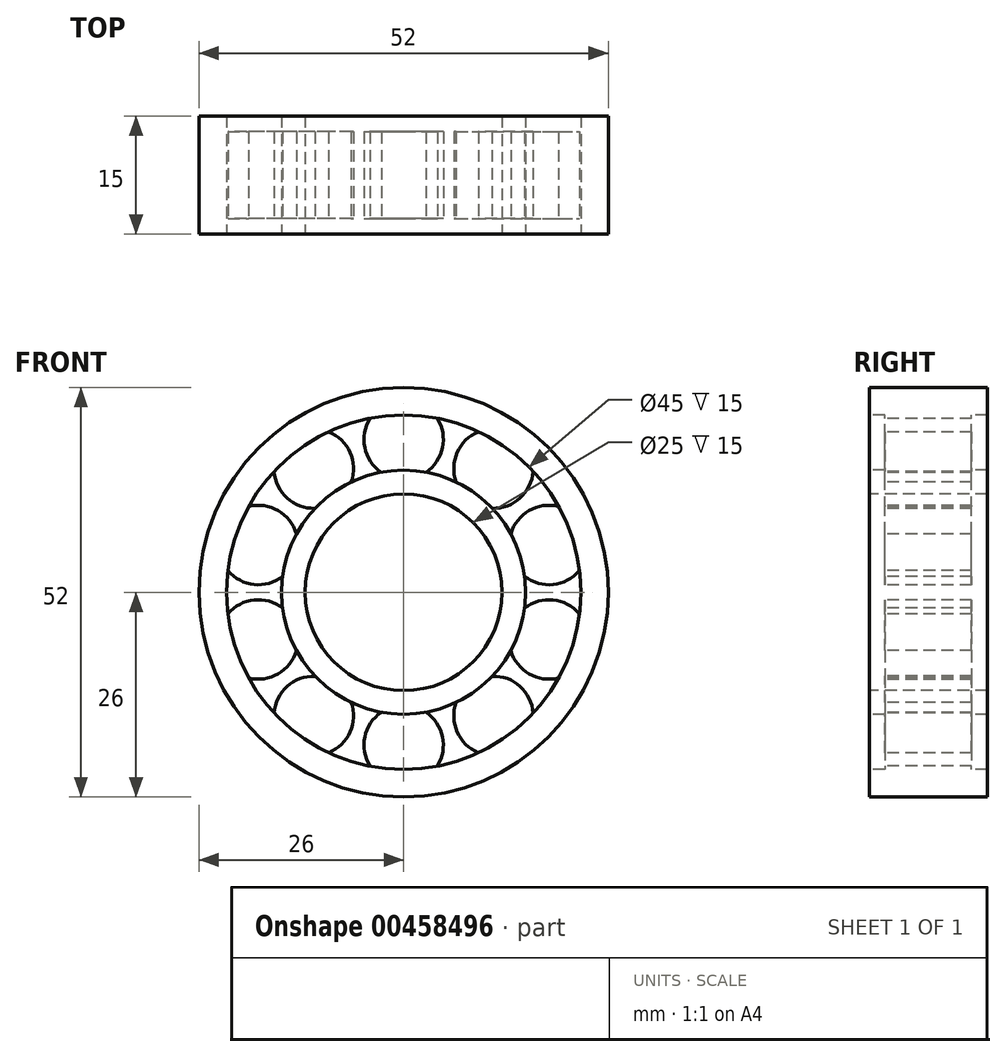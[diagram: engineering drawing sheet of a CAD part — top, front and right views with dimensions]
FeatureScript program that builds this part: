
annotation { "Feature Type Name" : "Feature", "Feature Type Description" : "" }
export const myFeature = defineFeature(function(context is Context, id is Id, definition is map)
    precondition{}
    {
        {
            var Q0;
            Q0=qCreatedBy(makeId("Front.planeOp"),FACE);
            var sketch = newSketch(context, id + "F0", { "sketchPlane" : qUnion([Q0])});
            skCircle(sketch, "E0", {"center": v(0, 0) * mm, "radius": 12.5 * mm});
            skCircle(sketch, "E1", {"center": v(0, 0) * mm, "radius": 26 * mm});
            skLineSegment(sketch, "E2.anchor2", {"start": v(0, -14.42) * mm, "end": v(0, -15.5) * mm, "construction": true});
            skPoint(sketch, "E3.orphan", {"position": v(9.11, 12.54) * mm});
            skPoint(sketch, "E4.orphan", {"position": v(14.74, 4.79) * mm});
            skPoint(sketch, "E5.orphan", {"position": v(14.74, -4.79) * mm});
            skPoint(sketch, "E6.orphan", {"position": v(9.11, -12.54) * mm});
            skPoint(sketch, "E7.orphan", {"position": v(0, -22.5) * mm});
            skPoint(sketch, "E8.orphan", {"position": v(0, 22.5) * mm});
            skPoint(sketch, "E2.anchor1.end.orphan", {"position": v(0, 15.5) * mm});
            skCircle(sketch, "E9", {"center": v(0, 0) * mm, "radius": 15.5 * mm});
            skCircle(sketch, "E10", {"center": v(0, 0) * mm, "radius": 22.5 * mm});
            skSolve(sketch);
        }
        {
            var Q0;
            Q0=makeQuery(id+"F0.imprint","IMPRINT",FACE,{"disambiguationData":[TD([[makeQuery(id+"F0.imprint","IMPRINT",EDGE,{"derivedFrom":sQuery(id+"F0.wireOp",EDGE,"E1")}),1.0]])]});
            extrude(context, id + "F1", {"entities" : qUnion([Q0]), "oppositeDirection" : true, "depth" : 15 * mm, "offsetDistance" : 25 * mm});
        }
        {
            var Q0;
            Q0=qCreatedBy(makeId("Front.planeOp"),FACE);
            cPlane(context, id + "F2", {"entities" : qUnion([Q0]), "cplaneType" : CPlaneType.OFFSET, "offset" : 2 * mm, "oppositeDirection" : true, "width" : 150 * mm, "height" : 150 * mm});
        }
        {
            var Q0;
            Q0=qCreatedBy(id+"F2.planeOp",FACE);
            var sketch = newSketch(context, id + "F3", { "sketchPlane" : qUnion([Q0])});
            skCircle(sketch, "E11", {"center": v(0, -19.42) * mm, "radius": 5.04 * mm});
            skCircle(sketch, "E12.1.0", {"center": v(11.41, -15.7) * mm, "radius": 5.04 * mm});
            skCircle(sketch, "E12.2.0", {"center": v(18.47, -6) * mm, "radius": 5.04 * mm});
            skCircle(sketch, "E12.3.0", {"center": v(18.47, 6) * mm, "radius": 5.04 * mm});
            skCircle(sketch, "E12.4.0", {"center": v(11.41, 15.7) * mm, "radius": 5.04 * mm});
            skCircle(sketch, "E12.5.0", {"center": v(0, 19.42) * mm, "radius": 5.04 * mm});
            skCircle(sketch, "E12.6.0", {"center": v(-11.41, 15.7) * mm, "radius": 5.04 * mm});
            skCircle(sketch, "E12.7.0", {"center": v(-18.47, 6) * mm, "radius": 5.04 * mm});
            skCircle(sketch, "E12.8.0", {"center": v(-18.47, -6) * mm, "radius": 5.04 * mm});
            skCircle(sketch, "E12.9.0", {"center": v(-11.41, -15.7) * mm, "radius": 5.04 * mm});
            skPoint(sketch, "E12.center", {"position": v(0, 0) * mm});
            skSolve(sketch);
        }
        {
            var Q0;
            Q0 = qSketchRegion(id + "F3", true);
            extrude(context, id + "F4", {"entities" : qUnion([Q0]), "operationType" : NewBodyOperationType.ADD, "oppositeDirection" : true, "depth" : 11 * mm});
        }
        {
            var Q0;
            Q0=makeQuery(id+"F0.imprint","IMPRINT",FACE,{"disambiguationData":[TD([[makeQuery(id+"F0.imprint","IMPRINT",EDGE,{"derivedFrom":sQuery(id+"F0.wireOp",EDGE,"E0")}),-1.0]])]});
            extrude(context, id + "F5", {"entities" : qUnion([Q0]), "operationType" : NewBodyOperationType.ADD, "oppositeDirection" : true, "depth" : 15 * mm});
        }
    });
